# Revit family: BC_Hitachi_RAS-3HVRC2_LOD400
name_source: partatom
category: Equipement de génie climatique
revit_build: Autodesk Revit 2018 (Build: 20181015_0930(x64)
units: mm (PartAtom-declared; Revit-internal decimal feet)

## family parameters
Basée sur le plan de construction = Non
Cote de connecteur circulaire = Utiliser le diamètre
Couper avec des vides une fois chargée = Non
Numéro OmniClass = 23.75.70.17
Partagée = Non
Point de calcul de pièce = Non
Titre OmniClass = Water Heated and Cooled Terminal Heating and Cooling Units
Toujours verticalement = Oui
Type d'élément = Normal

## types (1)
- RAS-3HVRC2
    Actuator cables = 2 x 0,75mm² + GND
    Additional refrigerant charge needed per meter = 15 g/m
    Applicable voltage - Umax = 253 V
    Applicable voltage - Umin = 207 V
    BC_OBJECT_ID = 215284
    BC_OBJECT_VERSION = #37
    BC_VARIANT_ID = 561968
    CB = 20 A
    Commentaires du type = Yutaki 3HP outdoor unit (R32)
    Description = Yutaki 3HP outdoor unit (R32)
    ELB = 2/40/30
    ErP website = https://www.hitachiaircon-erpactive.com
    Fabricant = Hitachi
    Frequency = 50 Hz
    Global Warming Potential (GWP) (kg CO2 equi/UF) = 675
    Height difference between OU & IU (higher OU) = 30000.00 mm
    Height difference between OU & IU (lower OU) = 20000.00 mm
    MATERIAL = Metal
    MC = 17 A
    Maximum Current = 16 A
    Maximum chargless piping length = 10000.00 mm
    Maximum piping length (additional refrigerant needed) = 40.00 m
    Miminum piping length = 3000.00 mm
    Modèle = Yutaki 3HP outdoor unit (R32)
    Net Weight = 44.00 kg
    Nominal Voltage = 230 V
    Number of Phases = 1
    Overall Depth = 300.00 mm
    Overall Height = 629.00 mm
    Overall Width = 898.00 mm
    Piping diameter (gas)  ≤ 30 = 15.88 mm
    Piping diameter (gas)  ≥ 30 = 15.88 mm
    Piping diameter (liquid) ≤ 30 = 6.35 mm
    Piping diameter (liquid) ≥30 = 9.52 mm
    Power supply cables = 2 x 4,0 mm² +GND
    Reference = RAS-3HVRC2
    Refrigerant Type = R32
    Refrigerant charge before shipment = 1.30 kg
    Refrigerant pipes connection - gas pipe diameter = 15.88 mm
    Refrigerant pipes connection - liquid pipe diameter = 9.52 mm
    Sound power OU = 69
    Transmitting cables = 2 x 0,75mm² (*Shielded cable)
    Working range (DHW) (°C) = -20~35
    Working range (cooling) (°C) = 10~46
    Working range (heating) (°C) = -20~25
    Zmax (Ω) = 0.4
